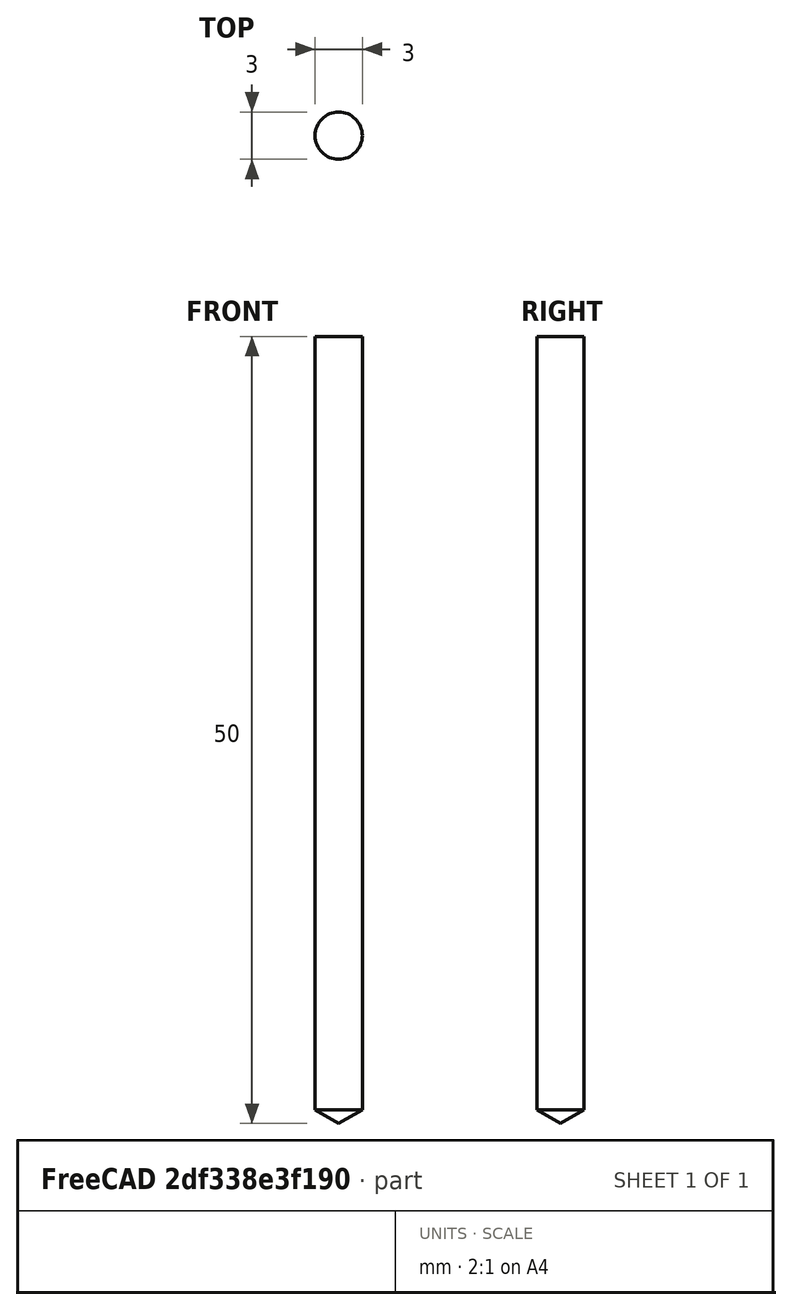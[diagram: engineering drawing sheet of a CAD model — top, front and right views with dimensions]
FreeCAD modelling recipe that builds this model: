
FCSTD DOCUMENT  (FreeCAD 0.19R20874 (Git))
Label: drill
License: All rights reserved
LicenseURL: http://en.wikipedia.org/wiki/All_rights_reserved
objects: Sketcher::SketchObject×1, PartDesign::Revolution×1, PartDesign::Body×1
note: 4 computed .brp shape members not serialized (recipe doc carries the construction recipe); baked Part::Feature solids carry a one-line shape summary decoded from their .brp

FEATURE [Sketcher::SketchObject] Sketch
  MapMode = 5
  Placement = pos=(0,0,0) rot=(1,0,0;1.5708rad)
  Support = -> [XZ_Plane]
  sketch-geometry (7):
    g0: LineSegment StartX=0 StartY=50 StartZ=0 EndX=0 EndY=-2.03286e-11 EndZ=0
    g1: LineSegment StartX=0 StartY=-2.03286e-11 StartZ=0 EndX=1.5 EndY=0.883568 EndZ=0
    g2: LineSegment StartX=1.5 StartY=0.883568 StartZ=0 EndX=1.5 EndY=50 EndZ=0
    g3: LineSegment StartX=1.5 StartY=50 StartZ=0 EndX=0 EndY=50 EndZ=0
    g4: LineSegment [constr] StartX=1.5 StartY=0.883568 StartZ=0 EndX=-1.5 EndY=0.883568 EndZ=0
    g5: LineSegment [constr] StartX=-1.5 StartY=0.883568 StartZ=0 EndX=0 EndY=-2.03287e-11 EndZ=0
    g6: LineSegment [constr] StartX=0 StartY=-2.03286e-11 StartZ=0 EndX=1.5 EndY=0.883568 EndZ=0
  constraints (17):
    c: Vertical(g0)
    c: Coincident(g0,g1)
    c: Coincident(g1,g2)
    c: Vertical(g2)
    c: Coincident(g2,g3)
    c: Horizontal(g3)
    c: Coincident(g0,g3)
    c: Coincident(g4,g5)
    c: Coincident(g5,g6)
    c: Coincident(g6,g4)
    c: Coincident(g1,g4)
    c: Coincident(g5,g0)
    c: Symmetric(g4,g1,g0)
    c: Angle(g1,g5) = 2.07694  'TipAngle; Full angle of the drill tip'
    c: DistanceX(g4,g4) = 3  'Diameter; Drill bit diameter'
    c: DistanceY(g0,g0) = 50  'Length; Overall length of the drillbit'
    c: Coincident(g0,g-1)
FEATURE [PartDesign::Revolution] Revolution
  AllowMultiFace = false
  Angle = 360
  Axis = (0,-2e-16,1)
  Base = (0,0,0)
  Placement = pos=(0,0,0) rot=(1,0,0;1.5708rad)
  Profile = -> Sketch
  ReferenceAxis = -> Sketch [V_Axis]
  Reversed = true
FEATURE [PartDesign::Body] Body  label="Drill"
  Group = -> [Sketch,Revolution]
  Origin = -> Origin
  Tip = -> Revolution
